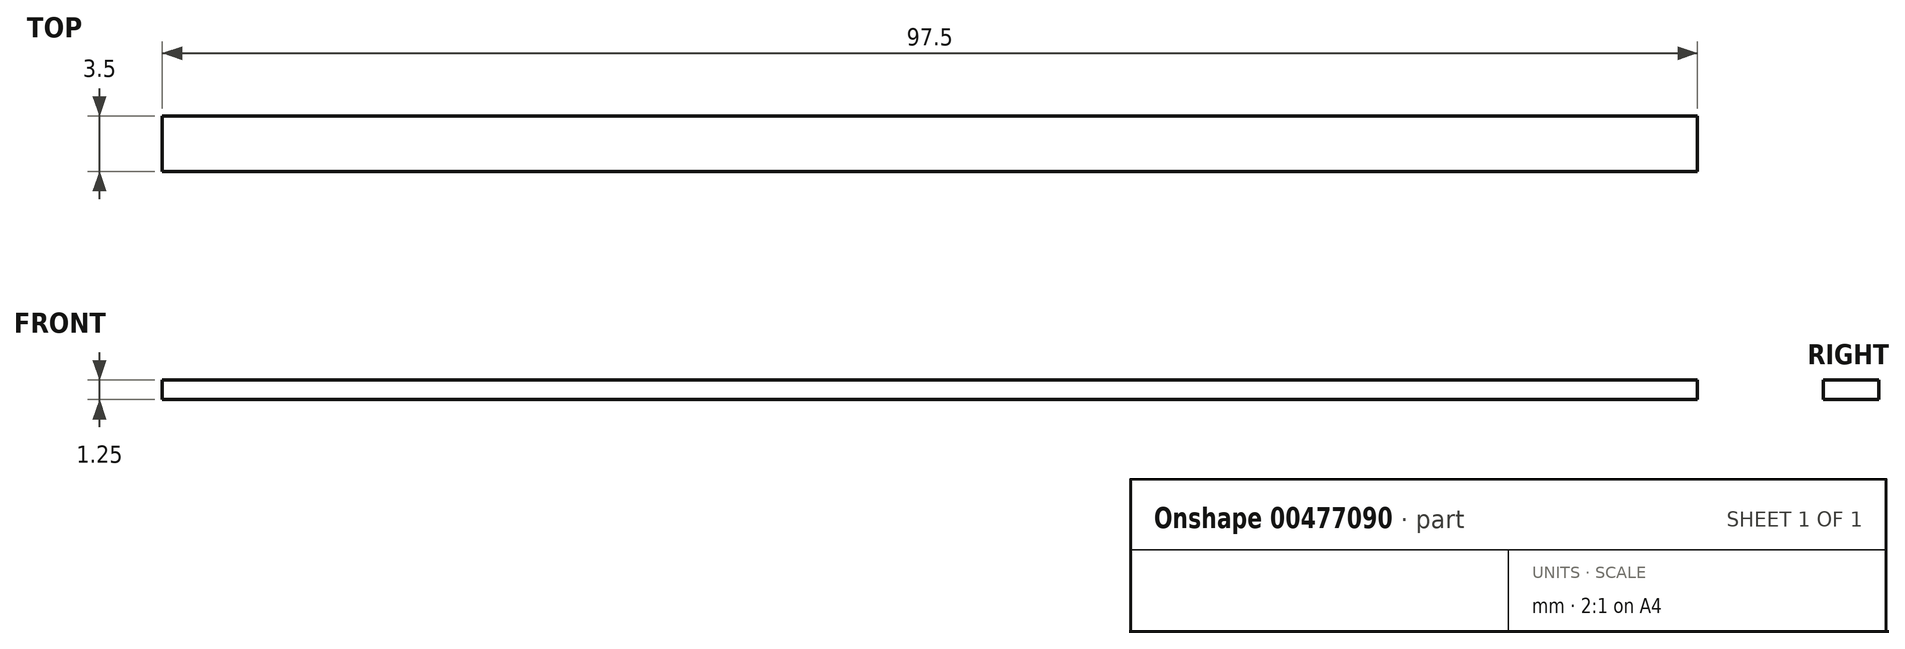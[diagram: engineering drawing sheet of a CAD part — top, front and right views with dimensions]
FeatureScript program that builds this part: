
annotation { "Feature Type Name" : "Feature", "Feature Type Description" : "" }
export const myFeature = defineFeature(function(context is Context, id is Id, definition is map)
    precondition{}
    {
        {
            var Q0;
            Q0=qCreatedBy(makeId("Top.planeOp"),FACE);
            var sketch = newSketch(context, id + "F0", { "sketchPlane" : qUnion([Q0])});
            skLineSegment(sketch, "E0.bottom", {"start": v(-49.98, -11.26) * mm, "end": v(47.52, -11.26) * mm});
            skLineSegment(sketch, "E0.top", {"start": v(-49.98, -14.76) * mm, "end": v(47.52, -14.76) * mm});
            skLineSegment(sketch, "E0.left", {"start": v(-49.98, -11.26) * mm, "end": v(-49.98, -14.76) * mm});
            skLineSegment(sketch, "E0.right", {"start": v(47.52, -11.26) * mm, "end": v(47.52, -14.76) * mm});
            skSolve(sketch);
        }
        {
            var Q0;
            Q0=qSketchRegion(id+"F0",true);
            extrude(context, id + "F1", {"entities" : qUnion([Q0]), "depth" : 1.25 * mm});
        }
    });
